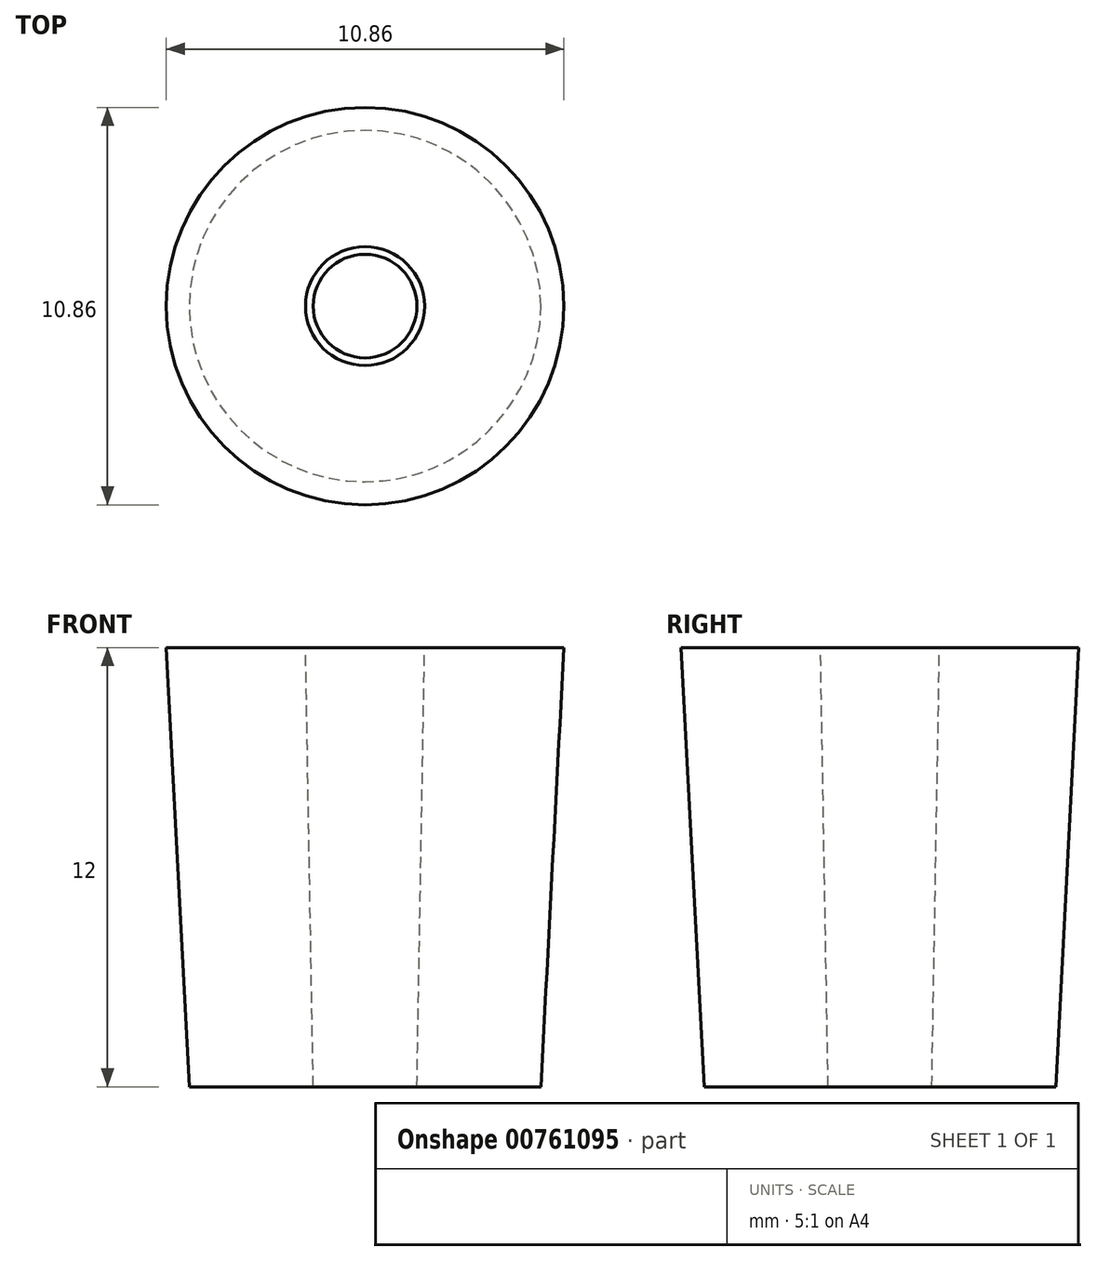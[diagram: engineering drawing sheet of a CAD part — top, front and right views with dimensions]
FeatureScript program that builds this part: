
annotation { "Feature Type Name" : "Feature", "Feature Type Description" : "" }
export const myFeature = defineFeature(function(context is Context, id is Id, definition is map)
    precondition{}
    {
        {
            var Q0;
            Q0=qCreatedBy(makeId("Top.planeOp"),FACE);
            var sketch = newSketch(context, id + "F0", { "sketchPlane" : qUnion([Q0])});
            skCircle(sketch, "E0", {"center": v(0, 0) * mm, "radius": 4.8 * mm});
            skSolve(sketch);
        }
        {
            var Q0;
            Q0=makeQuery(id+"F0.imprint","IMPRINT",FACE,{"disambiguationData":[TD([[makeQuery(id+"F0.imprint","IMPRINT",EDGE,{"derivedFrom":sQuery(id+"F0.wireOp",EDGE,"E0")}),1.0]])]});
            extrude(context, id + "F1", {"entities" : qUnion([Q0]), "depth" : 12 * mm, "offsetDistance" : 25 * mm, "hasDraft" : true, "draftAngle" : 3 * degree});
        }
        {
            var Q0;
            Q0=makeQuery(id+"F1.opExtrude","CAP_FACE",FACE,{"disambiguationData":[OSD([sQuery(id+"F0.wireOp",EDGE,"E0")])],"isStart":false});
            var sketch = newSketch(context, id + "F2", { "sketchPlane" : qUnion([Q0])});
            skCircle(sketch, "E1", {"center": v(0, 0) * mm, "radius": 1.63 * mm});
            skSolve(sketch);
        }
        {
            var Q0;
            Q0=makeQuery(id+"F2.imprint","IMPRINT",FACE,{"disambiguationData":[TD([[makeQuery(id+"F2.imprint","IMPRINT",EDGE,{"derivedFrom":sQuery(id+"F2.wireOp",EDGE,"E1")}),1.0]])]});
            extrude(context, id + "F3", {"entities" : qUnion([Q0]), "operationType" : NewBodyOperationType.REMOVE, "oppositeDirection" : true, "depth" : 12 * mm, "offsetDistance" : 25 * mm, "hasDraft" : true, "draftAngle" : 1 * degree, "draftPullDirection" : true});
        }
    });
